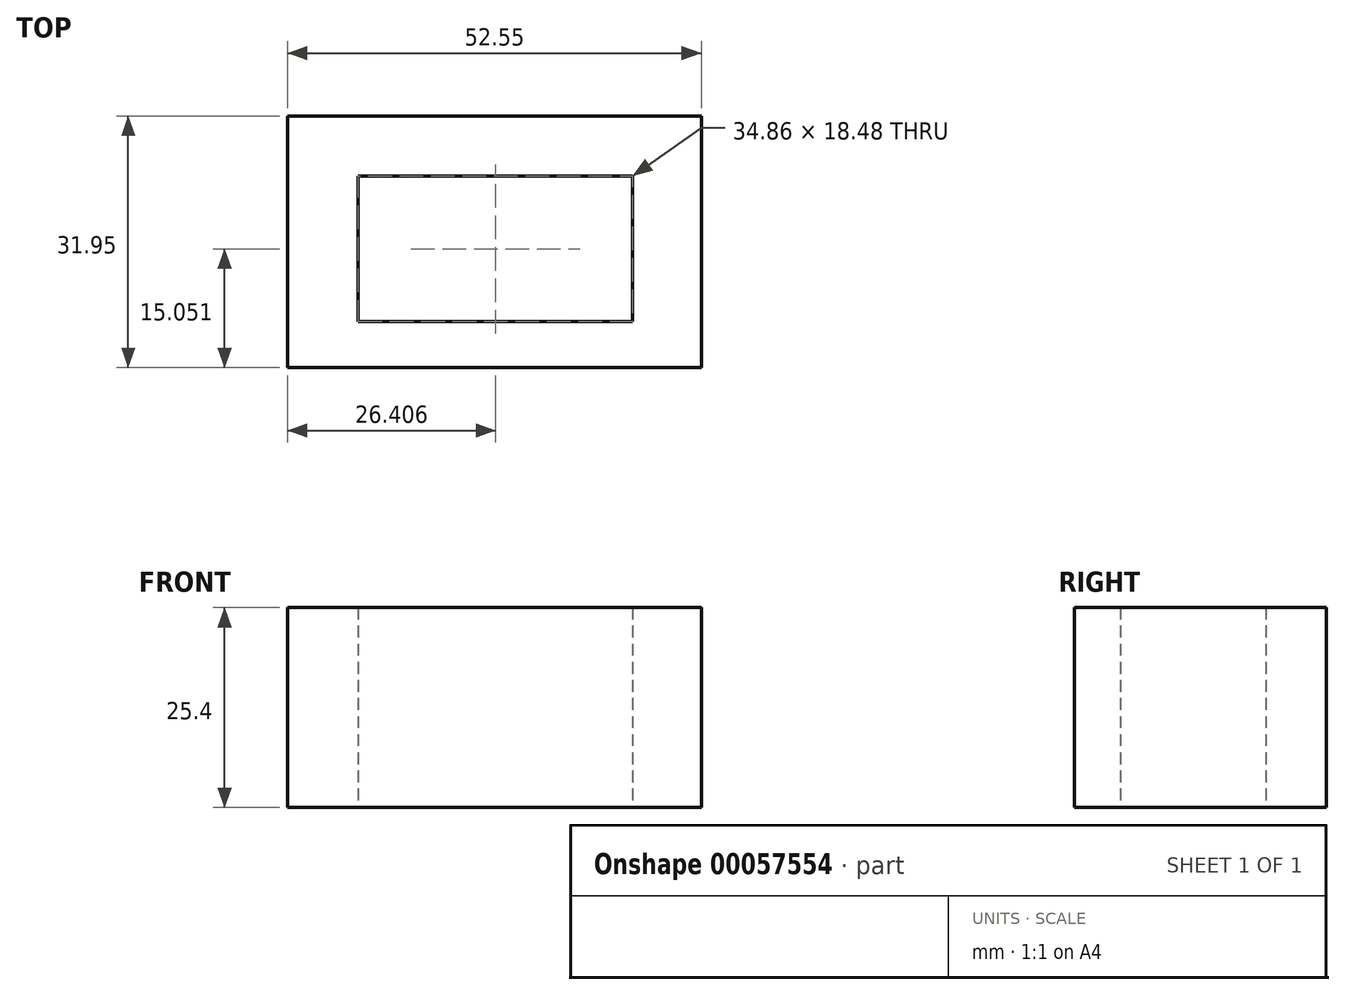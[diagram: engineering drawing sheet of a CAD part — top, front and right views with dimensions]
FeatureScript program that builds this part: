
annotation { "Feature Type Name" : "Feature", "Feature Type Description" : "" }
export const myFeature = defineFeature(function(context is Context, id is Id, definition is map)
    precondition{}
    {
        {
            var Q0;
            Q0=qCreatedBy(makeId("Top.planeOp"),FACE);
            var sketch = newSketch(context, id + "F0", { "sketchPlane" : qUnion([Q0])});
            skLineSegment(sketch, "E0.bottom", {"start": v(0, 0) * mm, "end": v(52.55, 0) * mm});
            skLineSegment(sketch, "E0.top", {"start": v(0, 31.95) * mm, "end": v(52.55, 31.95) * mm});
            skLineSegment(sketch, "E0.left", {"start": v(0, 0) * mm, "end": v(0, 31.95) * mm});
            skLineSegment(sketch, "E0.right", {"start": v(52.55, 0) * mm, "end": v(52.55, 31.95) * mm});
            skLineSegment(sketch, "E1.bottom", {"start": v(8.98, 24.3) * mm, "end": v(43.83, 24.3) * mm});
            skLineSegment(sketch, "E1.top", {"start": v(8.98, 5.8) * mm, "end": v(43.83, 5.8) * mm});
            skLineSegment(sketch, "E1.left", {"start": v(8.98, 24.3) * mm, "end": v(8.98, 5.8) * mm});
            skLineSegment(sketch, "E1.right", {"start": v(43.83, 24.3) * mm, "end": v(43.83, 5.8) * mm});
            skSolve(sketch);
        }
        {
            var Q0;
            Q0 = qSketchRegion(id + "F0", true);
            extrude(context, id + "F1", {"entities" : qUnion([Q0]), "depth" : 25.4 * mm});
        }
    });
